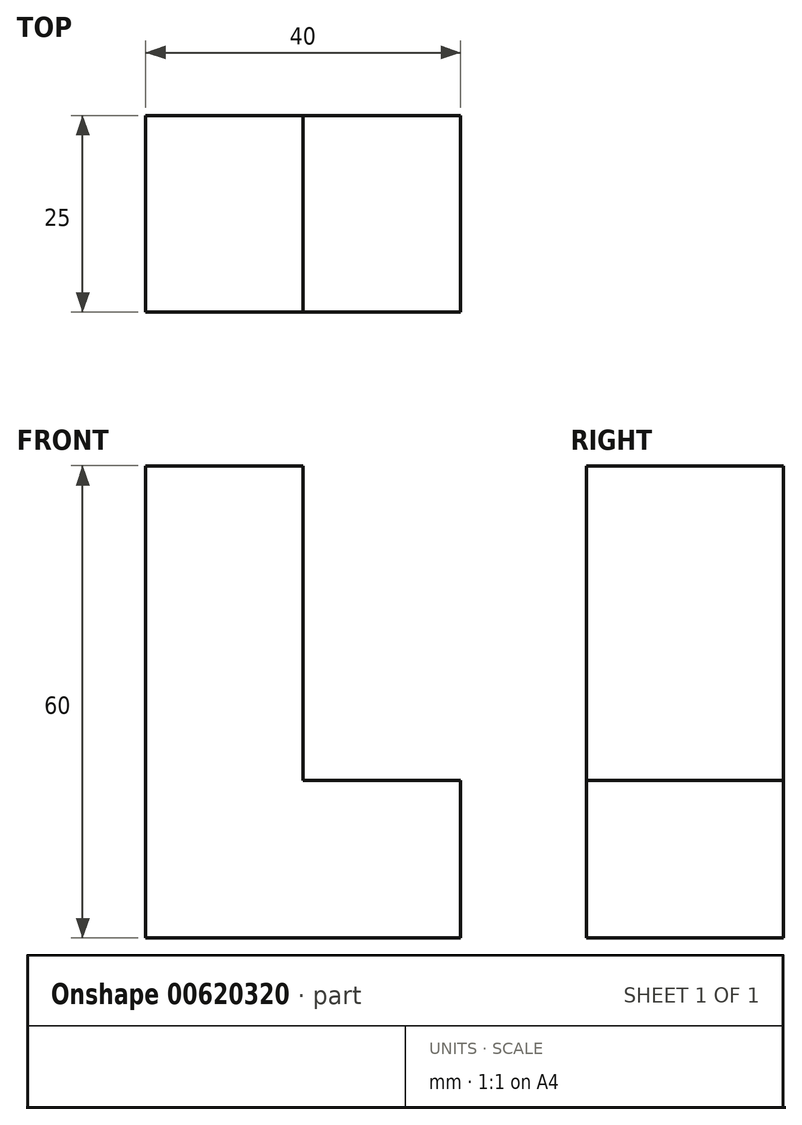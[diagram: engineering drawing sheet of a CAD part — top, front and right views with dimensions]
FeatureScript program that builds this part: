
annotation { "Feature Type Name" : "Feature", "Feature Type Description" : "" }
export const myFeature = defineFeature(function(context is Context, id is Id, definition is map)
    precondition{}
    {
        {
            var Q0;
            Q0=qCreatedBy(makeId("Front.planeOp"),FACE);
            var sketch = newSketch(context, id + "F0", { "sketchPlane" : qUnion([Q0])});
            skLineSegment(sketch, "E0", {"start": v(-20, 48.42) * mm, "end": v(-20, -11.58) * mm});
            skLineSegment(sketch, "E1", {"start": v(-20, -11.58) * mm, "end": v(0, -11.58) * mm});
            skLineSegment(sketch, "E2", {"start": v(0, -11.58) * mm, "end": v(0, 48.42) * mm});
            skLineSegment(sketch, "E3", {"start": v(-20, 48.42) * mm, "end": v(0, 48.42) * mm});
            skLineSegment(sketch, "E4", {"start": v(0, 8.42) * mm, "end": v(20, 8.42) * mm});
            skLineSegment(sketch, "E5", {"start": v(20, -11.58) * mm, "end": v(0, -11.58) * mm});
            skLineSegment(sketch, "E6", {"start": v(20, -11.58) * mm, "end": v(20, 8.42) * mm});
            skSolve(sketch);
        }
        {
            var Q0;
            Q0 = qSketchRegion(id + "F0", true);
            extrude(context, id + "F1", {"entities" : qUnion([Q0]), "depth" : 25 * mm, "offsetDistance" : 25 * mm});
        }
    });
